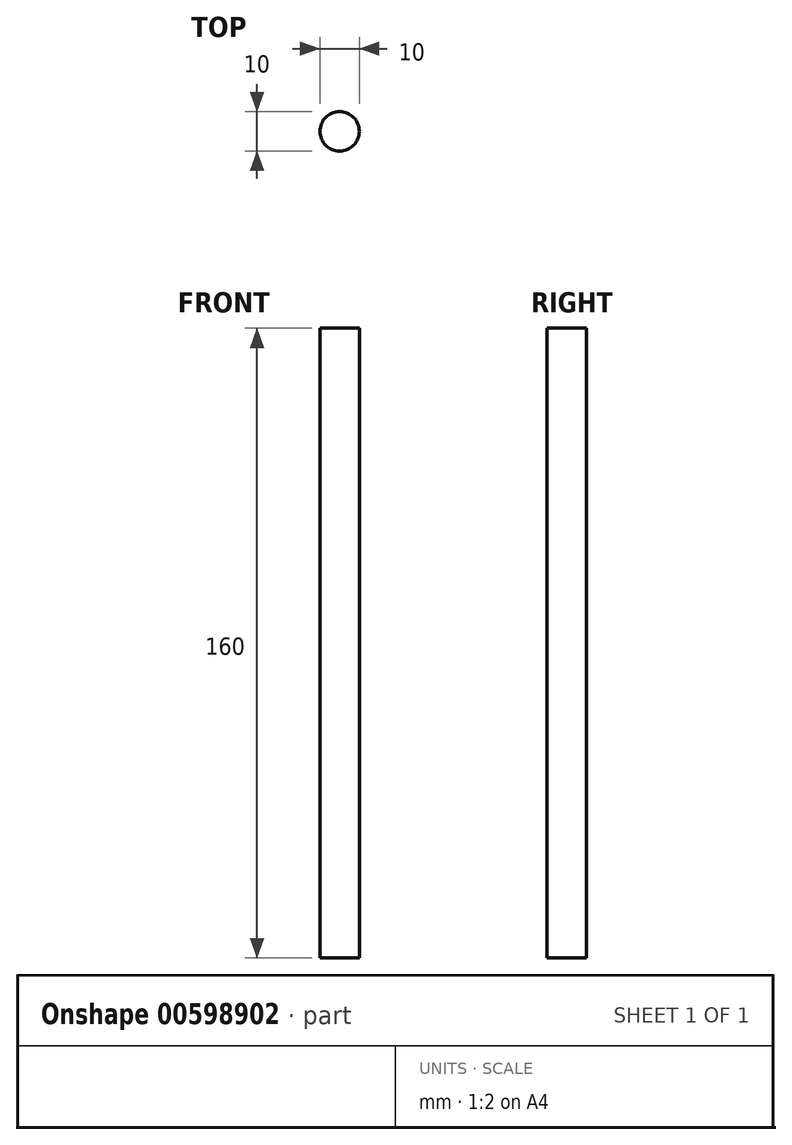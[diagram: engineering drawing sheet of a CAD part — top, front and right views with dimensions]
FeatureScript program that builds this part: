
annotation { "Feature Type Name" : "Feature", "Feature Type Description" : "" }
export const myFeature = defineFeature(function(context is Context, id is Id, definition is map)
    precondition{}
    {
        {
            var Q0;
            Q0=qCreatedBy(makeId("Top.planeOp"),FACE);
            var sketch = newSketch(context, id + "F0", { "sketchPlane" : qUnion([Q0])});
            skCircle(sketch, "E0", {"center": v(0, 0) * mm, "radius": 5 * mm});
            skSolve(sketch);
        }
        {
            var Q0;
            Q0 = qSketchRegion(id + "F0", true);
            extrude(context, id + "F1", {"entities" : qUnion([Q0]), "depth" : 160 * mm, "offsetDistance" : 25 * mm});
        }
    });
